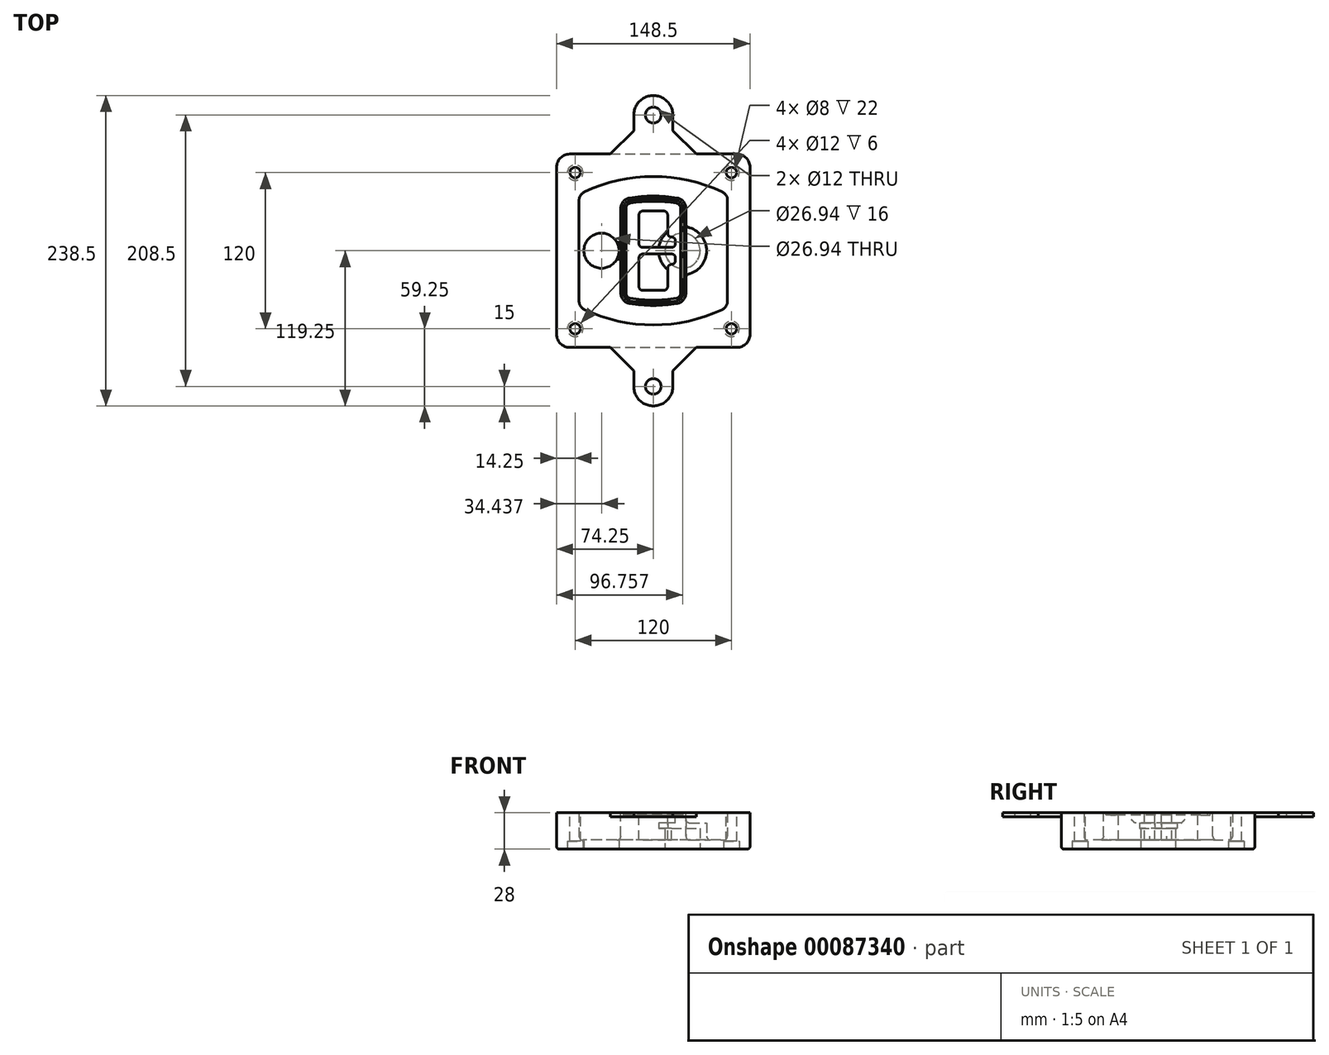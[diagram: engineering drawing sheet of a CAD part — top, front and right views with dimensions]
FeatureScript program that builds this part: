
annotation { "Feature Type Name" : "Feature", "Feature Type Description" : "" }
export const myFeature = defineFeature(function(context is Context, id is Id, definition is map)
    precondition{}
    {
        {
            var Q0;
            Q0=qCreatedBy(makeId("Top.planeOp"),FACE);
            var sketch = newSketch(context, id + "F0", { "sketchPlane" : qUnion([Q0])});
            skPoint(sketch, "E0.rect.middle", {"position": v(0, 0) * mm});
            skLineSegment(sketch, "E1.bottom", {"start": v(-64.25, -74.25) * mm, "end": v(64.25, -74.25) * mm});
            skLineSegment(sketch, "E1.top", {"start": v(-64.25, 74.25) * mm, "end": v(64.25, 74.25) * mm});
            skLineSegment(sketch, "E1.left", {"start": v(-74.25, -64.25) * mm, "end": v(-74.25, 64.25) * mm});
            skLineSegment(sketch, "E1.right", {"start": v(74.25, -64.25) * mm, "end": v(74.25, 64.25) * mm});
            skLineSegment(sketch, "E2", {"start": v(-74.25, 74.25) * mm, "end": v(74.25, -74.25) * mm, "construction": true});
            skLineSegment(sketch, "E3", {"start": v(74.25, 74.25) * mm, "end": v(-74.25, -74.25) * mm, "construction": true});
            skCircle(sketch, "E4", {"center": v(-60, 60) * mm, "radius": 4 * mm});
            skCircle(sketch, "E5", {"center": v(60, 60) * mm, "radius": 4 * mm});
            skCircle(sketch, "E6", {"center": v(60, -60) * mm, "radius": 4 * mm});
            skCircle(sketch, "E7", {"center": v(-60, -60) * mm, "radius": 4 * mm});
            skLineSegment(sketch, "E8", {"start": v(-60, 60) * mm, "end": v(60, 60) * mm, "construction": true});
            skLineSegment(sketch, "E9", {"start": v(60, 60) * mm, "end": v(60, -60) * mm, "construction": true});
            skLineSegment(sketch, "E10", {"start": v(60, -60) * mm, "end": v(-60, -60) * mm, "construction": true});
            skLineSegment(sketch, "E11", {"start": v(-60, -60) * mm, "end": v(-60, 60) * mm, "construction": true});
            skLineSegment(sketch, "E12", {"start": v(-60, 38.83) * mm, "end": v(-60, -38.83) * mm});
            skLineSegment(sketch, "E13", {"start": v(60, 38.83) * mm, "end": v(60, -38.83) * mm});
            skArc(sketch, "E14", {"start": v(54.26, 47.88) * mm, "mid": v(0, 60) * mm, "end": v(-54.26, 47.88) * mm});
            skArc(sketch, "E15", {"start": v(-54.26, -47.88) * mm, "mid": v(0, -60) * mm, "end": v(54.26, -47.88) * mm});
            skLineSegment(sketch, "E16", {"start": v(-60, 0) * mm, "end": v(60, 0) * mm, "construction": true});
            skPoint(sketch, "E17.visualSharp", {"position": v(-60, -45) * mm});
            skArc(sketch, "E17.filletArc", {"start": v(-60, -38.83) * mm, "mid": v(-58.44, -44.2) * mm, "end": v(-54.26, -47.88) * mm});
            skPoint(sketch, "E18.visualSharp", {"position": v(-60, 45) * mm});
            skArc(sketch, "E18.filletArc", {"start": v(-54.26, 47.88) * mm, "mid": v(-58.44, 44.2) * mm, "end": v(-60, 38.83) * mm});
            skPoint(sketch, "E19.visualSharp", {"position": v(60, 45) * mm});
            skArc(sketch, "E19.filletArc", {"start": v(60, 38.83) * mm, "mid": v(58.44, 44.2) * mm, "end": v(54.26, 47.88) * mm});
            skPoint(sketch, "E20.visualSharp", {"position": v(60, -45) * mm});
            skArc(sketch, "E20.filletArc", {"start": v(54.26, -47.88) * mm, "mid": v(58.44, -44.2) * mm, "end": v(60, -38.83) * mm});
            skPoint(sketch, "E21.visualSharp", {"position": v(-74.25, 74.25) * mm});
            skArc(sketch, "E21.filletArc", {"start": v(-64.25, 74.25) * mm, "mid": v(-71.32, 71.32) * mm, "end": v(-74.25, 64.25) * mm});
            skPoint(sketch, "E22.visualSharp", {"position": v(74.25, 74.25) * mm});
            skArc(sketch, "E22.filletArc", {"start": v(74.25, 64.25) * mm, "mid": v(71.32, 71.32) * mm, "end": v(64.25, 74.25) * mm});
            skPoint(sketch, "E23.visualSharp", {"position": v(74.25, -74.25) * mm});
            skArc(sketch, "E23.filletArc", {"start": v(64.25, -74.25) * mm, "mid": v(71.32, -71.32) * mm, "end": v(74.25, -64.25) * mm});
            skPoint(sketch, "E24.visualSharp", {"position": v(-74.25, -74.25) * mm});
            skArc(sketch, "E24.filletArc", {"start": v(-74.25, -64.25) * mm, "mid": v(-71.32, -71.32) * mm, "end": v(-64.25, -74.25) * mm});
            skArc(sketch, "E25.0", {"start": v(57, 38.83) * mm, "mid": v(55.9, 42.58) * mm, "end": v(52.98, 45.17) * mm});
            skLineSegment(sketch, "E25.1", {"start": v(57, 38.83) * mm, "end": v(57, -38.83) * mm});
            skArc(sketch, "E25.2", {"start": v(52.98, -45.17) * mm, "mid": v(55.9, -42.58) * mm, "end": v(57, -38.83) * mm});
            skArc(sketch, "E25.3", {"start": v(-52.98, -45.17) * mm, "mid": v(0, -57) * mm, "end": v(52.98, -45.17) * mm});
            skArc(sketch, "E25.4", {"start": v(-57, -38.83) * mm, "mid": v(-55.9, -42.58) * mm, "end": v(-52.98, -45.17) * mm});
            skArc(sketch, "E25.5", {"start": v(52.98, 45.17) * mm, "mid": v(0, 57) * mm, "end": v(-52.98, 45.17) * mm});
            skLineSegment(sketch, "E25.6", {"start": v(-57, 38.83) * mm, "end": v(-57, -38.83) * mm});
            skArc(sketch, "E25.7", {"start": v(-52.98, 45.17) * mm, "mid": v(-55.9, 42.58) * mm, "end": v(-57, 38.83) * mm});
            skArc(sketch, "E26.0", {"start": v(-55.96, 51.5) * mm, "mid": v(-61.82, 46.33) * mm, "end": v(-64, 38.83) * mm});
            skArc(sketch, "E26.1", {"start": v(55.96, 51.5) * mm, "mid": v(0, 64) * mm, "end": v(-55.96, 51.5) * mm});
            skArc(sketch, "E26.2", {"start": v(64, 38.83) * mm, "mid": v(61.82, 46.33) * mm, "end": v(55.96, 51.5) * mm});
            skLineSegment(sketch, "E26.3", {"start": v(64, 38.83) * mm, "end": v(64, -38.83) * mm});
            skArc(sketch, "E26.4", {"start": v(55.96, -51.5) * mm, "mid": v(61.82, -46.33) * mm, "end": v(64, -38.83) * mm});
            skLineSegment(sketch, "E26.5", {"start": v(-64, 38.83) * mm, "end": v(-64, -38.83) * mm});
            skArc(sketch, "E26.6", {"start": v(-55.96, -51.5) * mm, "mid": v(0, -64) * mm, "end": v(55.96, -51.5) * mm});
            skArc(sketch, "E26.7", {"start": v(-64, -38.83) * mm, "mid": v(-61.82, -46.33) * mm, "end": v(-55.96, -51.5) * mm});
            skSolve(sketch);
        }
        {
            var Q0;
            Q0=makeQuery(id+"F0.imprint","IMPRINT",FACE,{"disambiguationData":[TD([[makeQuery(id+"F0.imprint","IMPRINT",EDGE,{"derivedFrom":sQuery(id+"F0.wireOp",EDGE,"E1.bottom")}),1.0]])]});
            var Q1;
            Q1=makeQuery(id+"F0.imprint","IMPRINT",FACE,{"disambiguationData":[TD([[makeQuery(id+"F0.imprint","IMPRINT",EDGE,{"derivedFrom":sQuery(id+"F0.wireOp",EDGE,"E12")}),1.0]])]});
            var Q2;
            Q2=makeQuery(id+"F0.imprint","IMPRINT",FACE,{"disambiguationData":[TD([[makeQuery(id+"F0.imprint","IMPRINT",EDGE,{"derivedFrom":sQuery(id+"F0.wireOp",EDGE,"E25.0")}),1.0]])]});
            var Q3;
            Q3=makeQuery(id+"F0.imprint","IMPRINT",FACE,{"disambiguationData":[TD([[makeQuery(id+"F0.imprint","IMPRINT",EDGE,{"derivedFrom":sQuery(id+"F0.wireOp",EDGE,"E12")}),-1.0]])]});
            extrude(context, id + "F1", {"entities" : qUnion([Q0, Q1, Q2, Q3]), "oppositeDirection" : true, "depth" : 25 * mm});
        }
        {
            var Q0;
            Q0=makeQuery(id+"F0.imprint","IMPRINT",FACE,{"disambiguationData":[TD([[makeQuery(id+"F0.imprint","IMPRINT",EDGE,{"derivedFrom":sQuery(id+"F0.wireOp",EDGE,"E12")}),1.0]])]});
            extrude(context, id + "F2", {"entities" : qUnion([Q0]), "operationType" : NewBodyOperationType.ADD, "depth" : 3 * mm});
        }
        {
            var Q0;
            Q0=makeQuery(id+"F0.imprint","IMPRINT",FACE,{"disambiguationData":[TD([[makeQuery(id+"F0.imprint","IMPRINT",EDGE,{"derivedFrom":sQuery(id+"F0.wireOp",EDGE,"E25.0")}),1.0]])]});
            extrude(context, id + "F3", {"entities" : qUnion([Q0]), "operationType" : NewBodyOperationType.REMOVE, "oppositeDirection" : true, "depth" : 18 * mm});
        }
        {
            var Q0;
            Q0=makeQuery(id+"F2.opExtrude","CAP_FACE",FACE,{"disambiguationData":[OSD([sQuery(id+"F0.wireOp",EDGE,"E12"),sQuery(id+"F0.wireOp",EDGE,"E13"),sQuery(id+"F0.wireOp",EDGE,"E14"),sQuery(id+"F0.wireOp",EDGE,"E15"),sQuery(id+"F0.wireOp",EDGE,"E17.filletArc"),sQuery(id+"F0.wireOp",EDGE,"E18.filletArc"),sQuery(id+"F0.wireOp",EDGE,"E19.filletArc"),sQuery(id+"F0.wireOp",EDGE,"E20.filletArc"),sQuery(id+"F0.wireOp",EDGE,"E25.0"),sQuery(id+"F0.wireOp",EDGE,"E25.1"),sQuery(id+"F0.wireOp",EDGE,"E25.2"),sQuery(id+"F0.wireOp",EDGE,"E25.3"),sQuery(id+"F0.wireOp",EDGE,"E25.4"),sQuery(id+"F0.wireOp",EDGE,"E25.5"),sQuery(id+"F0.wireOp",EDGE,"E25.6"),sQuery(id+"F0.wireOp",EDGE,"E25.7")])],"isStart":false});
            var sketch = newSketch(context, id + "F4", { "sketchPlane" : qUnion([Q0])});
            skArc(sketch, "E27.0", {"start": v(-18.34, -40.45) * mm, "mid": v(0, -42) * mm, "end": v(18.34, -40.45) * mm});
            skArc(sketch, "E28.0", {"start": v(18.34, 40.45) * mm, "mid": v(0, 42) * mm, "end": v(-18.34, 40.45) * mm});
            skLineSegment(sketch, "E29", {"start": v(-25, 32.57) * mm, "end": v(-25, -32.57) * mm});
            skLineSegment(sketch, "E30", {"start": v(25, 32.57) * mm, "end": v(25, -32.57) * mm});
            skLineSegment(sketch, "E31", {"start": v(-25, 39.1) * mm, "end": v(25, 39.1) * mm, "construction": true});
            skLineSegment(sketch, "E32", {"start": v(-25, -39.1) * mm, "end": v(25, -39.1) * mm, "construction": true});
            skPoint(sketch, "E33.visualSharp", {"position": v(-25, 39.1) * mm});
            skArc(sketch, "E33.filletArc", {"start": v(-18.34, 40.45) * mm, "mid": v(-23.11, 37.73) * mm, "end": v(-25, 32.57) * mm});
            skPoint(sketch, "E34.visualSharp", {"position": v(25, 39.1) * mm});
            skArc(sketch, "E34.filletArc", {"start": v(25, 32.57) * mm, "mid": v(23.11, 37.73) * mm, "end": v(18.34, 40.45) * mm});
            skPoint(sketch, "E35.visualSharp", {"position": v(25, -39.1) * mm});
            skArc(sketch, "E35.filletArc", {"start": v(18.34, -40.45) * mm, "mid": v(23.11, -37.73) * mm, "end": v(25, -32.57) * mm});
            skPoint(sketch, "E36.visualSharp", {"position": v(-25, -39.1) * mm});
            skArc(sketch, "E36.filletArc", {"start": v(-25, -32.57) * mm, "mid": v(-23.11, -37.73) * mm, "end": v(-18.34, -40.45) * mm});
            skArc(sketch, "E37.0", {"start": v(52.98, 45.17) * mm, "mid": v(0, 57) * mm, "end": v(-52.98, 45.17) * mm});
            skArc(sketch, "E37.1", {"start": v(-52.98, 45.17) * mm, "mid": v(-55.9, 42.58) * mm, "end": v(-57, 38.83) * mm});
            skLineSegment(sketch, "E37.2", {"start": v(-57, 38.83) * mm, "end": v(-57, -38.83) * mm});
            skArc(sketch, "E37.3", {"start": v(-57, -38.83) * mm, "mid": v(-55.9, -42.58) * mm, "end": v(-52.98, -45.17) * mm});
            skArc(sketch, "E37.4", {"start": v(-52.98, -45.17) * mm, "mid": v(0, -57) * mm, "end": v(52.98, -45.17) * mm});
            skArc(sketch, "E37.5", {"start": v(52.98, -45.17) * mm, "mid": v(55.9, -42.58) * mm, "end": v(57, -38.83) * mm});
            skLineSegment(sketch, "E37.6", {"start": v(57, 38.83) * mm, "end": v(57, -38.83) * mm});
            skArc(sketch, "E37.7", {"start": v(57, 38.83) * mm, "mid": v(55.9, 42.58) * mm, "end": v(52.98, 45.17) * mm});
            skLineSegment(sketch, "E38.0", {"start": v(23, 32.57) * mm, "end": v(23, -32.57) * mm});
            skArc(sketch, "E38.1", {"start": v(18, -38.48) * mm, "mid": v(21.58, -36.44) * mm, "end": v(23, -32.57) * mm});
            skArc(sketch, "E38.2", {"start": v(-18, -38.48) * mm, "mid": v(0, -40) * mm, "end": v(18, -38.48) * mm});
            skArc(sketch, "E38.3", {"start": v(-23, -32.57) * mm, "mid": v(-21.58, -36.44) * mm, "end": v(-18, -38.48) * mm});
            skLineSegment(sketch, "E38.4", {"start": v(-23, 32.57) * mm, "end": v(-23, -32.57) * mm});
            skArc(sketch, "E38.5", {"start": v(23, 32.57) * mm, "mid": v(21.58, 36.44) * mm, "end": v(18, 38.48) * mm});
            skArc(sketch, "E38.6", {"start": v(-18, 38.48) * mm, "mid": v(-21.58, 36.44) * mm, "end": v(-23, 32.57) * mm});
            skArc(sketch, "E38.7", {"start": v(18, 38.48) * mm, "mid": v(0, 40) * mm, "end": v(-18, 38.48) * mm});
            skArc(sketch, "E39.0", {"start": v(21, 32.57) * mm, "mid": v(20.06, 35.15) * mm, "end": v(17.67, 36.5) * mm});
            skLineSegment(sketch, "E39.1", {"start": v(21, 32.57) * mm, "end": v(21, -32.57) * mm});
            skArc(sketch, "E39.2", {"start": v(17.67, -36.5) * mm, "mid": v(20.06, -35.15) * mm, "end": v(21, -32.57) * mm});
            skArc(sketch, "E39.3", {"start": v(-17.67, -36.5) * mm, "mid": v(0, -38) * mm, "end": v(17.67, -36.5) * mm});
            skArc(sketch, "E39.4", {"start": v(-21, -32.57) * mm, "mid": v(-20.06, -35.15) * mm, "end": v(-17.67, -36.5) * mm});
            skArc(sketch, "E39.5", {"start": v(17.67, 36.5) * mm, "mid": v(0, 38) * mm, "end": v(-17.67, 36.5) * mm});
            skLineSegment(sketch, "E39.6", {"start": v(-21, 32.57) * mm, "end": v(-21, -32.57) * mm});
            skArc(sketch, "E39.7", {"start": v(-17.67, 36.5) * mm, "mid": v(-20.06, 35.15) * mm, "end": v(-21, 32.57) * mm});
            skLineSegment(sketch, "E40", {"start": v(-25, 0) * mm, "end": v(25, 0) * mm, "construction": true});
            skLineSegment(sketch, "E41", {"start": v(-11, 5.5) * mm, "end": v(-11, 27.5) * mm});
            skLineSegment(sketch, "E42", {"start": v(-8, 30.5) * mm, "end": v(8, 30.5) * mm});
            skLineSegment(sketch, "E43", {"start": v(11, 27.5) * mm, "end": v(11, 13.5) * mm});
            skLineSegment(sketch, "E44", {"start": v(14, 10.5) * mm, "end": v(14, 10.5) * mm});
            skLineSegment(sketch, "E45", {"start": v(17, 7.5) * mm, "end": v(17, 5.5) * mm});
            skLineSegment(sketch, "E46", {"start": v(14, 2.5) * mm, "end": v(-8, 2.5) * mm});
            skPoint(sketch, "E47.visualSharp", {"position": v(-11, 30.5) * mm});
            skArc(sketch, "E47.filletArc", {"start": v(-8, 30.5) * mm, "mid": v(-10.12, 29.62) * mm, "end": v(-11, 27.5) * mm});
            skPoint(sketch, "E48.visualSharp", {"position": v(11, 30.5) * mm});
            skArc(sketch, "E48.filletArc", {"start": v(11, 27.5) * mm, "mid": v(10.12, 29.62) * mm, "end": v(8, 30.5) * mm});
            skPoint(sketch, "E49.visualSharp", {"position": v(11, 10.5) * mm});
            skArc(sketch, "E49.filletArc", {"start": v(11, 13.5) * mm, "mid": v(11.88, 11.38) * mm, "end": v(14, 10.5) * mm});
            skPoint(sketch, "E50.visualSharp", {"position": v(17, 10.5) * mm});
            skArc(sketch, "E50.filletArc", {"start": v(17, 7.5) * mm, "mid": v(16.12, 9.62) * mm, "end": v(14, 10.5) * mm});
            skPoint(sketch, "E51.visualSharp", {"position": v(17, 2.5) * mm});
            skArc(sketch, "E51.filletArc", {"start": v(14, 2.5) * mm, "mid": v(16.12, 3.38) * mm, "end": v(17, 5.5) * mm});
            skPoint(sketch, "E52.visualSharp", {"position": v(-11, 2.5) * mm});
            skArc(sketch, "E52.filletArc", {"start": v(-11, 5.5) * mm, "mid": v(-10.12, 3.38) * mm, "end": v(-8, 2.5) * mm});
            skLineSegment(sketch, "E53.0.MirrorCS", {"start": v(14, -2.5) * mm, "end": v(-8, -2.5) * mm});
            skArc(sketch, "E54.0.MirrorCS", {"start": v(-11, -5.5) * mm, "mid": v(-10.12, -3.38) * mm, "end": v(-8, -2.5) * mm});
            skLineSegment(sketch, "E55.0.MirrorCS", {"start": v(-11, -5.5) * mm, "end": v(-11, -27.5) * mm});
            skArc(sketch, "E56.0.MirrorCS", {"start": v(-8, -30.5) * mm, "mid": v(-10.12, -29.62) * mm, "end": v(-11, -27.5) * mm});
            skLineSegment(sketch, "E57.0.MirrorCS", {"start": v(-8, -30.5) * mm, "end": v(8, -30.5) * mm});
            skArc(sketch, "E58.0.MirrorCS", {"start": v(11, -27.5) * mm, "mid": v(10.12, -29.62) * mm, "end": v(8, -30.5) * mm});
            skLineSegment(sketch, "E59.0.MirrorCS", {"start": v(11, -27.5) * mm, "end": v(11, -13.5) * mm});
            skArc(sketch, "E60.0.MirrorCS", {"start": v(11, -13.5) * mm, "mid": v(11.88, -11.38) * mm, "end": v(14, -10.5) * mm});
            skArc(sketch, "E61.0.MirrorCS", {"start": v(17, -7.5) * mm, "mid": v(16.12, -9.62) * mm, "end": v(14, -10.5) * mm});
            skLineSegment(sketch, "E62.0.MirrorCS", {"start": v(17, -7.5) * mm, "end": v(17, -5.5) * mm});
            skArc(sketch, "E63.0.MirrorCS", {"start": v(14, -2.5) * mm, "mid": v(16.12, -3.38) * mm, "end": v(17, -5.5) * mm});
            skSolve(sketch);
        }
        {
            var Q0;
            Q0=makeQuery(id+"F4.imprint","IMPRINT",FACE,{"disambiguationData":[TD([[makeQuery(id+"F4.imprint","IMPRINT",EDGE,{"derivedFrom":sQuery(id+"F4.wireOp",EDGE,"E27.0")}),1.0]])]});
            var Q1;
            Q1=makeQuery(id+"F4.imprint","IMPRINT",FACE,{"disambiguationData":[TD([[makeQuery(id+"F4.imprint","IMPRINT",EDGE,{"derivedFrom":sQuery(id+"F4.wireOp",EDGE,"E38.0")}),-1.0]])]});
            var Q2;
            Q2=makeQuery(id+"F4.imprint","IMPRINT",FACE,{"disambiguationData":[TD([[makeQuery(id+"F4.imprint","IMPRINT",EDGE,{"derivedFrom":sQuery(id+"F4.wireOp",EDGE,"E39.0")}),1.0]])]});
            extrude(context, id + "F5", {"entities" : qUnion([Q0, Q1, Q2]), "operationType" : NewBodyOperationType.ADD, "endBound" : BoundingType.UP_TO_NEXT, "oppositeDirection" : true, "depth" : 25 * mm});
        }
        {
            var Q0;
            Q0=makeQuery(id+"F4.imprint","IMPRINT",FACE,{"disambiguationData":[TD([[makeQuery(id+"F4.imprint","IMPRINT",EDGE,{"derivedFrom":sQuery(id+"F4.wireOp",EDGE,"E38.0")}),-1.0]])]});
            extrude(context, id + "F6", {"entities" : qUnion([Q0]), "operationType" : NewBodyOperationType.REMOVE, "oppositeDirection" : true, "depth" : 2 * mm});
        }
        {
            var Q0;
            Q0=makeQuery(id+"F1.opExtrude","CAP_FACE",FACE,{"disambiguationData":[OSD([sQuery(id+"F0.wireOp",EDGE,"E1.bottom"),sQuery(id+"F0.wireOp",EDGE,"E1.top"),sQuery(id+"F0.wireOp",EDGE,"E1.left"),sQuery(id+"F0.wireOp",EDGE,"E1.right"),sQuery(id+"F0.wireOp",EDGE,"E4"),sQuery(id+"F0.wireOp",EDGE,"E5"),sQuery(id+"F0.wireOp",EDGE,"E6"),sQuery(id+"F0.wireOp",EDGE,"E7"),sQuery(id+"F0.wireOp",EDGE,"E21.filletArc"),sQuery(id+"F0.wireOp",EDGE,"E22.filletArc"),sQuery(id+"F0.wireOp",EDGE,"E23.filletArc"),sQuery(id+"F0.wireOp",EDGE,"E24.filletArc")])],"isStart":false});
            var sketch = newSketch(context, id + "F7", { "sketchPlane" : qUnion([Q0])});
            skCircle(sketch, "E64", {"center": v(22.5, 0) * mm, "radius": 13.47 * mm});
            skCircle(sketch, "E65", {"center": v(-39.81, 0) * mm, "radius": 13.47 * mm});
            skLineSegment(sketch, "E66", {"start": v(74.25, 0) * mm, "end": v(-74.25, 0) * mm});
            skCircle(sketch, "E67", {"center": v(22.5, 0) * mm, "radius": 18.47 * mm});
            skCircle(sketch, "E68", {"center": v(60, -60) * mm, "radius": 6 * mm});
            skCircle(sketch, "E69", {"center": v(-60, -60) * mm, "radius": 6 * mm});
            skCircle(sketch, "E70", {"center": v(-60, 60) * mm, "radius": 6 * mm});
            skCircle(sketch, "E71", {"center": v(60, 60) * mm, "radius": 6 * mm});
            skSolve(sketch);
        }
        {
            var Q0;
            {var subQ1=sQuery(id+"F7.wireOp",EDGE,"E66");var subQ4=sQuery(id+"F7.wireOp",EDGE,"E64");var subQ6=makeQuery(id+"F7.imprint","INTERSECT",VERTEX,{"disambiguationData":[OD(0.0)],"derivedFrom":[subQ4,subQ1]});Q0=makeQuery(id+"F7.imprint","IMPRINT",FACE,{"disambiguationData":[TD([[makeQuery(id+"F7.imprint","IMPRINT",EDGE,{"disambiguationData":[TD([[subQ6,-1.0]])],"derivedFrom":subQ4}),-1.0]])]});}
            var Q1;
            {var subQ0=sQuery(id+"F7.wireOp",EDGE,"E66");var subQ1=sQuery(id+"F7.wireOp",EDGE,"E64");var subQ3=makeQuery(id+"F7.imprint","INTERSECT",VERTEX,{"disambiguationData":[OD(0.0)],"derivedFrom":[subQ1,subQ0]});Q1=makeQuery(id+"F7.imprint","IMPRINT",FACE,{"disambiguationData":[TD([[makeQuery(id+"F7.imprint","IMPRINT",EDGE,{"disambiguationData":[TD([[subQ3,-1.0]])],"derivedFrom":subQ1}),1.0]])]});}
            var Q2;
            {var subQ0=sQuery(id+"F7.wireOp",EDGE,"E66");var subQ1=sQuery(id+"F7.wireOp",EDGE,"E64");var subQ3=makeQuery(id+"F7.imprint","INTERSECT",VERTEX,{"disambiguationData":[OD(0.0)],"derivedFrom":[subQ1,subQ0]});Q2=makeQuery(id+"F7.imprint","IMPRINT",FACE,{"disambiguationData":[TD([[makeQuery(id+"F7.imprint","IMPRINT",EDGE,{"disambiguationData":[TD([[subQ3,1.0]])],"derivedFrom":subQ1}),1.0]])]});}
            var Q3;
            {var subQ1=sQuery(id+"F7.wireOp",EDGE,"E66");var subQ4=sQuery(id+"F7.wireOp",EDGE,"E64");var subQ6=makeQuery(id+"F7.imprint","INTERSECT",VERTEX,{"disambiguationData":[OD(0.0)],"derivedFrom":[subQ4,subQ1]});Q3=makeQuery(id+"F7.imprint","IMPRINT",FACE,{"disambiguationData":[TD([[makeQuery(id+"F7.imprint","IMPRINT",EDGE,{"disambiguationData":[TD([[subQ6,1.0]])],"derivedFrom":subQ4}),-1.0]])]});}
            extrude(context, id + "F8", {"entities" : qUnion([Q0, Q1, Q2, Q3]), "operationType" : NewBodyOperationType.ADD, "oppositeDirection" : true, "depth" : 20 * mm});
        }
        {
            var Q0;
            {var subQ0=sQuery(id+"F7.wireOp",EDGE,"E66");var subQ1=sQuery(id+"F7.wireOp",EDGE,"E64");var subQ3=makeQuery(id+"F7.imprint","INTERSECT",VERTEX,{"disambiguationData":[OD(0.0)],"derivedFrom":[subQ1,subQ0]});Q0=makeQuery(id+"F7.imprint","IMPRINT",FACE,{"disambiguationData":[TD([[makeQuery(id+"F7.imprint","IMPRINT",EDGE,{"disambiguationData":[TD([[subQ3,-1.0]])],"derivedFrom":subQ1}),1.0]])]});}
            var Q1;
            {var subQ0=sQuery(id+"F7.wireOp",EDGE,"E66");var subQ1=sQuery(id+"F7.wireOp",EDGE,"E64");var subQ3=makeQuery(id+"F7.imprint","INTERSECT",VERTEX,{"disambiguationData":[OD(0.0)],"derivedFrom":[subQ1,subQ0]});Q1=makeQuery(id+"F7.imprint","IMPRINT",FACE,{"disambiguationData":[TD([[makeQuery(id+"F7.imprint","IMPRINT",EDGE,{"disambiguationData":[TD([[subQ3,1.0]])],"derivedFrom":subQ1}),1.0]])]});}
            extrude(context, id + "F9", {"entities" : qUnion([Q0, Q1]), "operationType" : NewBodyOperationType.REMOVE, "oppositeDirection" : true, "depth" : 16 * mm});
        }
        {
            var Q0;
            {var subQ0=sQuery(id+"F7.wireOp",EDGE,"E66");var subQ1=sQuery(id+"F7.wireOp",EDGE,"E65");var subQ3=makeQuery(id+"F7.imprint","INTERSECT",VERTEX,{"disambiguationData":[OD(0.0)],"derivedFrom":[subQ1,subQ0]});Q0=makeQuery(id+"F7.imprint","IMPRINT",FACE,{"disambiguationData":[TD([[makeQuery(id+"F7.imprint","IMPRINT",EDGE,{"disambiguationData":[TD([[subQ3,-1.0]])],"derivedFrom":subQ1}),1.0]])]});}
            var Q1;
            {var subQ0=sQuery(id+"F7.wireOp",EDGE,"E66");var subQ1=sQuery(id+"F7.wireOp",EDGE,"E65");var subQ3=makeQuery(id+"F7.imprint","INTERSECT",VERTEX,{"disambiguationData":[OD(0.0)],"derivedFrom":[subQ1,subQ0]});Q1=makeQuery(id+"F7.imprint","IMPRINT",FACE,{"disambiguationData":[TD([[makeQuery(id+"F7.imprint","IMPRINT",EDGE,{"disambiguationData":[TD([[subQ3,1.0]])],"derivedFrom":subQ1}),1.0]])]});}
            extrude(context, id + "F10", {"entities" : qUnion([Q0, Q1]), "operationType" : NewBodyOperationType.REMOVE, "oppositeDirection" : true, "depth" : 25 * mm});
        }
        {
            var Q0;
            Q0=makeQuery(id+"F7.imprint","IMPRINT",FACE,{"disambiguationData":[TD([[makeQuery(id+"F7.imprint","IMPRINT",EDGE,{"derivedFrom":sQuery(id+"F7.wireOp",EDGE,"E68")}),1.0]])]});
            var Q1;
            Q1=makeQuery(id+"F7.imprint","IMPRINT",FACE,{"disambiguationData":[TD([[makeQuery(id+"F7.imprint","IMPRINT",EDGE,{"derivedFrom":makeQuery(id+"F1.opExtrude","CAP_EDGE",EDGE,{"disambiguationData":[OSD([sQuery(id+"F0.wireOp",EDGE,"E5")])],"isStart":false})}),-1.0]])]});
            var Q2;
            Q2=makeQuery(id+"F7.imprint","IMPRINT",FACE,{"disambiguationData":[TD([[makeQuery(id+"F7.imprint","IMPRINT",EDGE,{"derivedFrom":sQuery(id+"F7.wireOp",EDGE,"E69")}),1.0]])]});
            var Q3;
            Q3=makeQuery(id+"F7.imprint","IMPRINT",FACE,{"disambiguationData":[TD([[makeQuery(id+"F7.imprint","IMPRINT",EDGE,{"derivedFrom":makeQuery(id+"F1.opExtrude","CAP_EDGE",EDGE,{"disambiguationData":[OSD([sQuery(id+"F0.wireOp",EDGE,"E4")])],"isStart":false})}),-1.0]])]});
            var Q4;
            Q4=makeQuery(id+"F7.imprint","IMPRINT",FACE,{"disambiguationData":[TD([[makeQuery(id+"F7.imprint","IMPRINT",EDGE,{"derivedFrom":sQuery(id+"F7.wireOp",EDGE,"E70")}),1.0]])]});
            var Q5;
            Q5=makeQuery(id+"F7.imprint","IMPRINT",FACE,{"disambiguationData":[TD([[makeQuery(id+"F7.imprint","IMPRINT",EDGE,{"derivedFrom":makeQuery(id+"F1.opExtrude","CAP_EDGE",EDGE,{"disambiguationData":[OSD([sQuery(id+"F0.wireOp",EDGE,"E7")])],"isStart":false})}),-1.0]])]});
            var Q6;
            Q6=makeQuery(id+"F7.imprint","IMPRINT",FACE,{"disambiguationData":[TD([[makeQuery(id+"F7.imprint","IMPRINT",EDGE,{"derivedFrom":sQuery(id+"F7.wireOp",EDGE,"E71")}),1.0]])]});
            var Q7;
            Q7=makeQuery(id+"F7.imprint","IMPRINT",FACE,{"disambiguationData":[TD([[makeQuery(id+"F7.imprint","IMPRINT",EDGE,{"derivedFrom":makeQuery(id+"F1.opExtrude","CAP_EDGE",EDGE,{"disambiguationData":[OSD([sQuery(id+"F0.wireOp",EDGE,"E6")])],"isStart":false})}),-1.0]])]});
            extrude(context, id + "F11", {"entities" : qUnion([Q0, Q1, Q2, Q3, Q4, Q5, Q6, Q7]), "operationType" : NewBodyOperationType.REMOVE, "oppositeDirection" : true, "depth" : 6 * mm});
        }
        {
            var Q0;
            Q0=makeQuery(id+"F9.boolean.opBoolean","COPY",FACE,{"derivedFrom":makeQuery(id+"F9.opExtrude","CAP_FACE",FACE,{"disambiguationData":[OSD([sQuery(id+"F7.wireOp",EDGE,"E64")])],"isStart":false})});
            var sketch = newSketch(context, id + "F12", { "sketchPlane" : qUnion([Q0])});
            skArc(sketch, "E72.0", {"start": v(11, 14.45) * mm, "mid": v(6.45, 9.13) * mm, "end": v(4.2, 2.5) * mm});
            skArc(sketch, "E72.1", {"start": v(4.2, -2.5) * mm, "mid": v(6.45, -9.13) * mm, "end": v(11, -14.45) * mm});
            skLineSegment(sketch, "E73", {"start": v(4.2, -2.5) * mm, "end": v(14, -2.5) * mm});
            skLineSegment(sketch, "E74.0", {"start": v(14, 2.5) * mm, "end": v(4.2, 2.5) * mm});
            skArc(sketch, "E74.1", {"start": v(14, 2.5) * mm, "mid": v(16.12, 3.38) * mm, "end": v(17, 5.5) * mm});
            skLineSegment(sketch, "E74.2", {"start": v(17, 7.5) * mm, "end": v(17, 5.5) * mm});
            skArc(sketch, "E74.3", {"start": v(17, 7.5) * mm, "mid": v(16.12, 9.62) * mm, "end": v(14, 10.5) * mm});
            skArc(sketch, "E74.4", {"start": v(11, 13.5) * mm, "mid": v(11.88, 11.38) * mm, "end": v(14, 10.5) * mm});
            skLineSegment(sketch, "E74.5", {"start": v(11, 14.45) * mm, "end": v(11, 13.5) * mm});
            skLineSegment(sketch, "E74.7", {"start": v(14, -2.5) * mm, "end": v(4.2, -2.5) * mm});
            skArc(sketch, "E74.8", {"start": v(14, -2.5) * mm, "mid": v(16.12, -3.38) * mm, "end": v(17, -5.5) * mm});
            skLineSegment(sketch, "E74.9", {"start": v(17, -7.5) * mm, "end": v(17, -5.5) * mm});
            skArc(sketch, "E74.10", {"start": v(17, -7.5) * mm, "mid": v(16.12, -9.62) * mm, "end": v(14, -10.5) * mm});
            skArc(sketch, "E74.11", {"start": v(11, -13.5) * mm, "mid": v(11.88, -11.38) * mm, "end": v(14, -10.5) * mm});
            skLineSegment(sketch, "E74.12", {"start": v(11, -14.45) * mm, "end": v(11, -13.5) * mm});
            skPoint(sketch, "E75.orphan", {"position": v(11, -27.5) * mm});
            skPoint(sketch, "E76.orphan", {"position": v(-8, -2.5) * mm});
            skPoint(sketch, "E77.orphan", {"position": v(-8, 2.5) * mm});
            skPoint(sketch, "E78.orphan", {"position": v(11, 27.5) * mm});
            skSolve(sketch);
        }
        {
            var Q0;
            {var subQ7=sQuery(id+"F12.wireOp",EDGE,"E72.0");var subQ14=sQuery(id+"F12.wireOp",EDGE,"E72.1");var subQ16=sQuery(id+"F12.wireOp",EDGE,"E74.1");var subQ18=sQuery(id+"F12.wireOp",EDGE,"E74.8");Q0=qUnion([makeQuery(id+"F12.imprint","IMPRINT",FACE,{"disambiguationData":[TD([[makeQuery(id+"F12.imprint","IMPRINT",EDGE,{"derivedFrom":subQ7}),1.0]])]}),makeQuery(id+"F12.imprint","IMPRINT",FACE,{"disambiguationData":[TD([[makeQuery(id+"F12.imprint","IMPRINT",EDGE,{"derivedFrom":subQ14}),1.0]])]}),makeQuery(id+"F12.imprint","IMPRINT",FACE,{"disambiguationData":[TD([[makeQuery(id+"F12.imprint","IMPRINT",EDGE,{"derivedFrom":subQ16}),1.0]])]}),makeQuery(id+"F12.imprint","IMPRINT",FACE,{"disambiguationData":[TD([[makeQuery(id+"F12.imprint","IMPRINT",EDGE,{"derivedFrom":subQ18}),-1.0]])]})]);}
            var Q1;
            Q1=makeQuery(id+"F5.boolean.opBoolean","SPLIT",FACE,{"disambiguationData":[TD([makeQuery(id+"F5.opExtrude","SWEPT_FACE",FACE,{"disambiguationData":[OSD([sQuery(id+"F4.wireOp",EDGE,"E41")])]})])],"derivedFrom":makeQuery(id+"F3.boolean.opBoolean","COPY",FACE,{"derivedFrom":makeQuery(id+"F3.opExtrude","CAP_FACE",FACE,{"disambiguationData":[OSD([sQuery(id+"F0.wireOp",EDGE,"E25.0"),sQuery(id+"F0.wireOp",EDGE,"E25.1"),sQuery(id+"F0.wireOp",EDGE,"E25.2"),sQuery(id+"F0.wireOp",EDGE,"E25.3"),sQuery(id+"F0.wireOp",EDGE,"E25.4"),sQuery(id+"F0.wireOp",EDGE,"E25.5"),sQuery(id+"F0.wireOp",EDGE,"E25.6"),sQuery(id+"F0.wireOp",EDGE,"E25.7")])],"isStart":false})})});
            extrude(context, id + "F13", {"entities" : qUnion([Q0]), "operationType" : NewBodyOperationType.REMOVE, "endBound" : BoundingType.UP_TO_SURFACE, "endBoundEntityFace" : qUnion([Q1]), "depth" : 25 * mm});
        }
        {
            var Q0;
            Q0=makeQuery(id+"F3.boolean.opBoolean","COPY",EDGE,{"derivedFrom":makeQuery(id+"F3.opExtrude","CAP_EDGE",EDGE,{"disambiguationData":[OSD([sQuery(id+"F0.wireOp",EDGE,"E25.6")])],"isStart":false})});
            var Q1;
            Q1=makeQuery(id+"F8.boolean.opBoolean","INTERSECT",EDGE,{"derivedFrom":[makeQuery(id+"F5.opExtrude","SWEPT_FACE",FACE,{"disambiguationData":[OSD([sQuery(id+"F4.wireOp",EDGE,"E30")])]}),makeQuery(id+"F8.opExtrude","CAP_FACE",FACE,{"disambiguationData":[OSD([sQuery(id+"F7.wireOp",EDGE,"E67")])],"isStart":false})]});
            var Q2;
            Q2=makeQuery(id+"F8.boolean.opBoolean","INTERSECT",EDGE,{"disambiguationData":[OD(1.0)],"derivedFrom":[makeQuery(id+"F5.opExtrude","SWEPT_FACE",FACE,{"disambiguationData":[OSD([sQuery(id+"F4.wireOp",EDGE,"E30")])]}),makeQuery(id+"F8.opExtrude","SWEPT_FACE",FACE,{"disambiguationData":[OSD([sQuery(id+"F7.wireOp",EDGE,"E67")])]})]});
            var Q3;
            {var subQ0=sQuery(id+"F4.wireOp",EDGE,"E30");Q3=makeQuery(id+"F8.boolean.opBoolean","SPLIT",EDGE,{"disambiguationData":[TD([makeQuery(id+"F5.opExtrude","SWEPT_FACE",FACE,{"disambiguationData":[OSD([sQuery(id+"F4.wireOp",EDGE,"E35.filletArc")])]})])],"derivedFrom":makeQuery(id+"F5.opExtrude","CAP_EDGE",EDGE,{"disambiguationData":[OSD([subQ0])],"isStart":false})});}
            var Q4;
            {var subQ0=sQuery(id+"F0.wireOp",EDGE,"E25.7");var subQ1=sQuery(id+"F0.wireOp",EDGE,"E25.1");var subQ2=sQuery(id+"F0.wireOp",EDGE,"E25.6");var subQ3=sQuery(id+"F0.wireOp",EDGE,"E25.5");var subQ4=sQuery(id+"F0.wireOp",EDGE,"E25.4");var subQ5=sQuery(id+"F0.wireOp",EDGE,"E25.0");var subQ6=sQuery(id+"F0.wireOp",EDGE,"E25.2");var subQ7=sQuery(id+"F0.wireOp",EDGE,"E25.3");Q4=makeQuery(id+"F8.boolean.opBoolean","INTERSECT",EDGE,{"derivedFrom":[makeQuery(id+"F5.boolean.opBoolean","SPLIT",FACE,{"disambiguationData":[TD([makeQuery(id+"F2.opExtrude","SWEPT_FACE",FACE,{"disambiguationData":[OSD([subQ5])]})])],"derivedFrom":makeQuery(id+"F3.boolean.opBoolean","COPY",FACE,{"derivedFrom":makeQuery(id+"F3.opExtrude","CAP_FACE",FACE,{"disambiguationData":[OSD([subQ5,subQ1,subQ6,subQ7,subQ4,subQ3,subQ2,subQ0])],"isStart":false})})}),makeQuery(id+"F8.opExtrude","SWEPT_FACE",FACE,{"disambiguationData":[OSD([sQuery(id+"F7.wireOp",EDGE,"E67")])]})]});}
            var Q5;
            Q5=makeQuery(id+"F8.boolean.opBoolean","INTERSECT",EDGE,{"disambiguationData":[OD(0.0)],"derivedFrom":[makeQuery(id+"F5.opExtrude","SWEPT_FACE",FACE,{"disambiguationData":[OSD([sQuery(id+"F4.wireOp",EDGE,"E30")])]}),makeQuery(id+"F8.opExtrude","SWEPT_FACE",FACE,{"disambiguationData":[OSD([sQuery(id+"F7.wireOp",EDGE,"E67")])]})]});
            fillet(context, id + "F14", {"entities" : qUnion([Q0, Q1, Q2, Q3, Q4, Q5]), "radius" : 3 * mm, "tangentPropagation" : true, "allowEdgeOverflow" : false});
        }
        {
            var Q0;
            Q0=makeQuery(id+"F1.opExtrude","CAP_EDGE",EDGE,{"disambiguationData":[OSD([sQuery(id+"F0.wireOp",EDGE,"E1.bottom")])],"isStart":false});
            fillet(context, id + "F15", {"entities" : qUnion([Q0]), "radius" : 2 * mm, "tangentPropagation" : true, "allowEdgeOverflow" : false});
        }
        {
            var Q0;
            {var subQ0=sQuery(id+"F0.wireOp",EDGE,"E22.filletArc");var subQ1=sQuery(id+"F0.wireOp",EDGE,"E7");var subQ2=sQuery(id+"F0.wireOp",EDGE,"E6");var subQ3=sQuery(id+"F0.wireOp",EDGE,"E5");var subQ4=sQuery(id+"F0.wireOp",EDGE,"E4");var subQ5=sQuery(id+"F0.wireOp",EDGE,"E1.bottom");var subQ6=sQuery(id+"F0.wireOp",EDGE,"E21.filletArc");var subQ7=sQuery(id+"F0.wireOp",EDGE,"E1.top");var subQ8=sQuery(id+"F0.wireOp",EDGE,"E1.left");var subQ9=sQuery(id+"F0.wireOp",EDGE,"E1.right");var subQ10=sQuery(id+"F0.wireOp",EDGE,"E23.filletArc");var subQ11=sQuery(id+"F0.wireOp",EDGE,"E24.filletArc");Q0=makeQuery(id+"F2.boolean.opBoolean","SPLIT",FACE,{"disambiguationData":[TD([makeQuery(id+"F1.opExtrude","SWEPT_FACE",FACE,{"disambiguationData":[OSD([subQ5])]})])],"derivedFrom":makeQuery(id+"F1.opExtrude","CAP_FACE",FACE,{"disambiguationData":[OSD([subQ5,subQ7,subQ8,subQ9,subQ4,subQ3,subQ2,subQ1,subQ6,subQ0,subQ10,subQ11])],"isStart":true})});}
            var sketch = newSketch(context, id + "F16", { "sketchPlane" : qUnion([Q0])});
            skCircle(sketch, "E79", {"center": v(0, 104.25) * mm, "radius": 6 * mm});
            skArc(sketch, "E80", {"start": v(0, 119.25) * mm, "mid": v(10.6, 114.86) * mm, "end": v(15, 104.25) * mm});
            skArc(sketch, "E81", {"start": v(-15, 104.24) * mm, "mid": v(-10.6, 114.85) * mm, "end": v(0, 119.25) * mm});
            skLineSegment(sketch, "E82", {"start": v(-15, 104.24) * mm, "end": v(-15, 92.24) * mm});
            skLineSegment(sketch, "E83", {"start": v(15, 104.25) * mm, "end": v(15, 92.25) * mm});
            skLineSegment(sketch, "E84", {"start": v(-15, 92.24) * mm, "end": v(-33, 74.25) * mm});
            skLineSegment(sketch, "E85", {"start": v(15, 92.25) * mm, "end": v(33, 74.25) * mm});
            skLineSegment(sketch, "E86", {"start": v(0, 104.25) * mm, "end": v(0, 74.25) * mm, "construction": true});
            skLineSegment(sketch, "E87", {"start": v(74.25, 0) * mm, "end": v(172.36, 0) * mm, "construction": true});
            skArc(sketch, "E88.MirrorCS", {"start": v(0, -119.25) * mm, "mid": v(10.6, -114.86) * mm, "end": v(15, -104.25) * mm});
            skArc(sketch, "E89.MirrorCS", {"start": v(-15, -104.24) * mm, "mid": v(-10.6, -114.85) * mm, "end": v(0, -119.25) * mm});
            skLineSegment(sketch, "E90.MirrorCS", {"start": v(-15, -104.24) * mm, "end": v(-15, -92.24) * mm});
            skLineSegment(sketch, "E91.MirrorCS", {"start": v(-15, -92.24) * mm, "end": v(-33, -74.25) * mm});
            skLineSegment(sketch, "E92.MirrorCS", {"start": v(0, -104.25) * mm, "end": v(0, -74.25) * mm, "construction": true});
            skCircle(sketch, "E93.MirrorC", {"center": v(0, -104.25) * mm, "radius": 6 * mm});
            skLineSegment(sketch, "E94.MirrorCS", {"start": v(15, -104.25) * mm, "end": v(15, -92.25) * mm});
            skLineSegment(sketch, "E95.MirrorCS", {"start": v(15, -92.25) * mm, "end": v(33, -74.25) * mm});
            skSolve(sketch);
        }
        {
            var Q0;
            Q0=makeQuery(id+"F16.imprint","IMPRINT",FACE,{"disambiguationData":[TD([[makeQuery(id+"F16.imprint","IMPRINT",EDGE,{"derivedFrom":sQuery(id+"F16.wireOp",EDGE,"E79")}),-1.0]])]});
            var Q1;
            Q1=makeQuery(id+"F16.imprint","IMPRINT",FACE,{"disambiguationData":[TD([[makeQuery(id+"F16.imprint","IMPRINT",EDGE,{"derivedFrom":sQuery(id+"F16.wireOp",EDGE,"E88.MirrorCS")}),1.0]])]});
            var Q2;
            Q2=makeQuery(id+"F16.imprint","IMPRINT",FACE,{"disambiguationData":[TD([[makeQuery(id+"F16.imprint","IMPRINT",EDGE,{"derivedFrom":makeQuery(id+"F1.opExtrude","CAP_EDGE",EDGE,{"disambiguationData":[OSD([sQuery(id+"F0.wireOp",EDGE,"E1.left")])],"isStart":true})}),-1.0]])]});
            var Q3;
            Q3=makeQuery(id+"F2.opExtrude","CAP_FACE",FACE,{"disambiguationData":[OSD([sQuery(id+"F0.wireOp",EDGE,"E12"),sQuery(id+"F0.wireOp",EDGE,"E13"),sQuery(id+"F0.wireOp",EDGE,"E14"),sQuery(id+"F0.wireOp",EDGE,"E15"),sQuery(id+"F0.wireOp",EDGE,"E17.filletArc"),sQuery(id+"F0.wireOp",EDGE,"E18.filletArc"),sQuery(id+"F0.wireOp",EDGE,"E19.filletArc"),sQuery(id+"F0.wireOp",EDGE,"E20.filletArc"),sQuery(id+"F0.wireOp",EDGE,"E25.0"),sQuery(id+"F0.wireOp",EDGE,"E25.1"),sQuery(id+"F0.wireOp",EDGE,"E25.2"),sQuery(id+"F0.wireOp",EDGE,"E25.3"),sQuery(id+"F0.wireOp",EDGE,"E25.4"),sQuery(id+"F0.wireOp",EDGE,"E25.5"),sQuery(id+"F0.wireOp",EDGE,"E25.6"),sQuery(id+"F0.wireOp",EDGE,"E25.7")])],"isStart":false});
            extrude(context, id + "F17", {"entities" : qUnion([Q0, Q1, Q2]), "operationType" : NewBodyOperationType.ADD, "endBound" : BoundingType.UP_TO_SURFACE, "endBoundEntityFace" : qUnion([Q3]), "depth" : 25 * mm});
        }
    });
